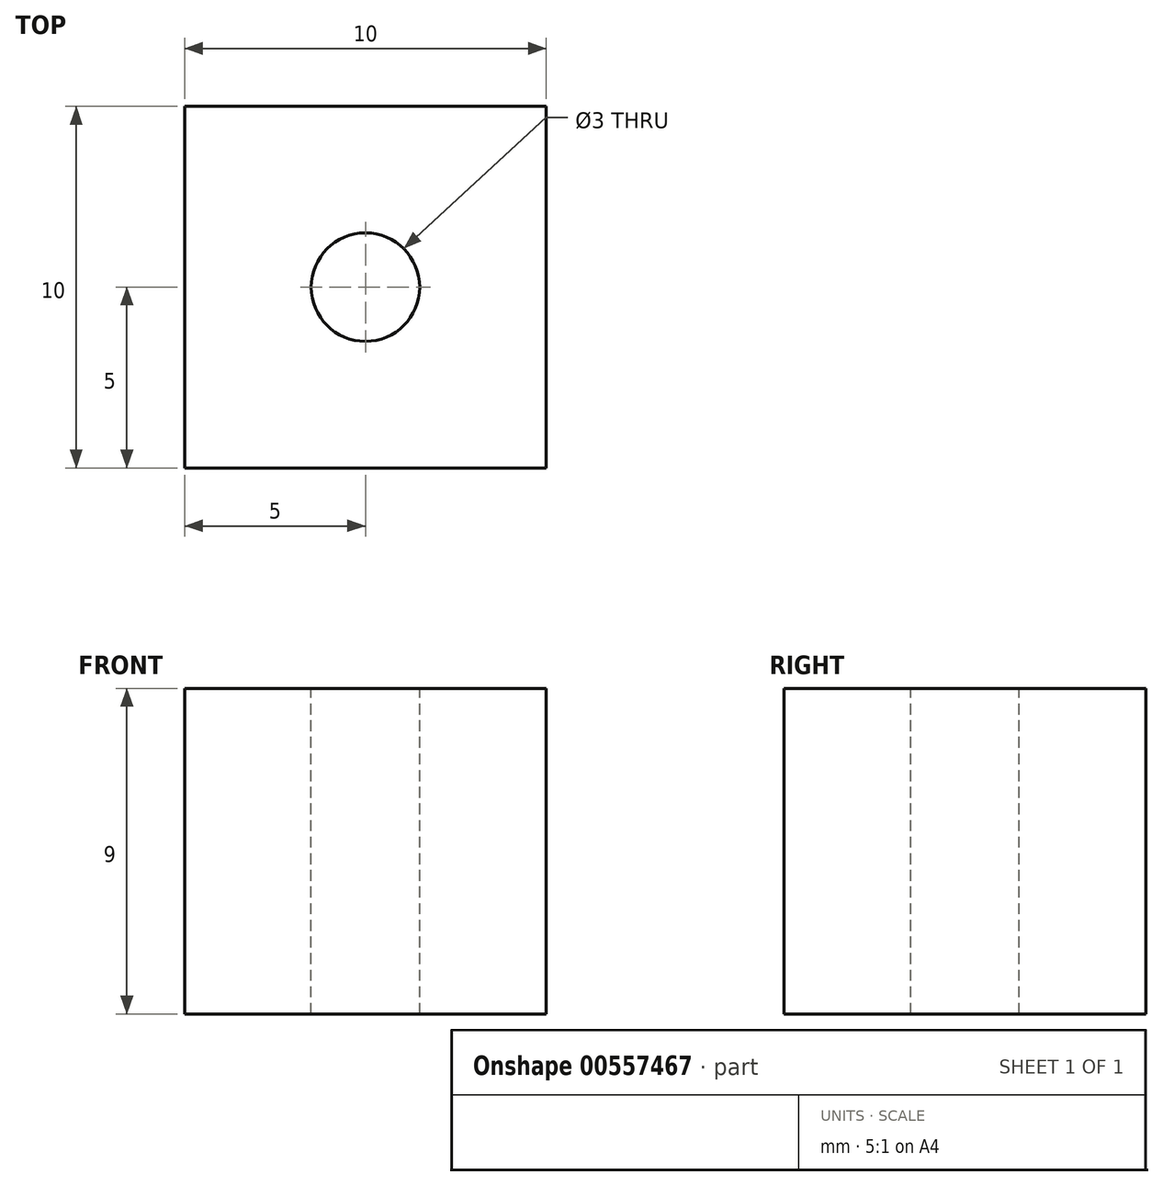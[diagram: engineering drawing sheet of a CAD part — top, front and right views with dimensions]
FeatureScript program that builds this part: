
annotation { "Feature Type Name" : "Feature", "Feature Type Description" : "" }
export const myFeature = defineFeature(function(context is Context, id is Id, definition is map)
    precondition{}
    {
        {
            var Q0;
            Q0=qCreatedBy(makeId("Top.planeOp"),FACE);
            var sketch = newSketch(context, id + "F0", { "sketchPlane" : qUnion([Q0])});
            skLineSegment(sketch, "E0.bottom", {"start": v(5, 5) * mm, "end": v(-5, 5) * mm});
            skLineSegment(sketch, "E0.top", {"start": v(5, -5) * mm, "end": v(-5, -5) * mm});
            skLineSegment(sketch, "E0.left", {"start": v(5, 5) * mm, "end": v(5, -5) * mm});
            skLineSegment(sketch, "E0.right", {"start": v(-5, 5) * mm, "end": v(-5, -5) * mm});
            skPoint(sketch, "E0.middle", {"position": v(0, 0) * mm});
            skCircle(sketch, "E1", {"center": v(0, 0) * mm, "radius": 1.5 * mm});
            skSolve(sketch);
        }
        {
            var Q0;
            Q0=makeQuery(id+"F0.imprint","IMPRINT",FACE,{"disambiguationData":[TD([[makeQuery(id+"F0.imprint","IMPRINT",EDGE,{"derivedFrom":sQuery(id+"F0.wireOp",EDGE,"E0.bottom")}),1.0]])]});
            extrude(context, id + "F1", {"entities" : qUnion([Q0]), "oppositeDirection" : true, "depth" : 9 * mm, "offsetDistance" : 25 * mm});
        }
    });
